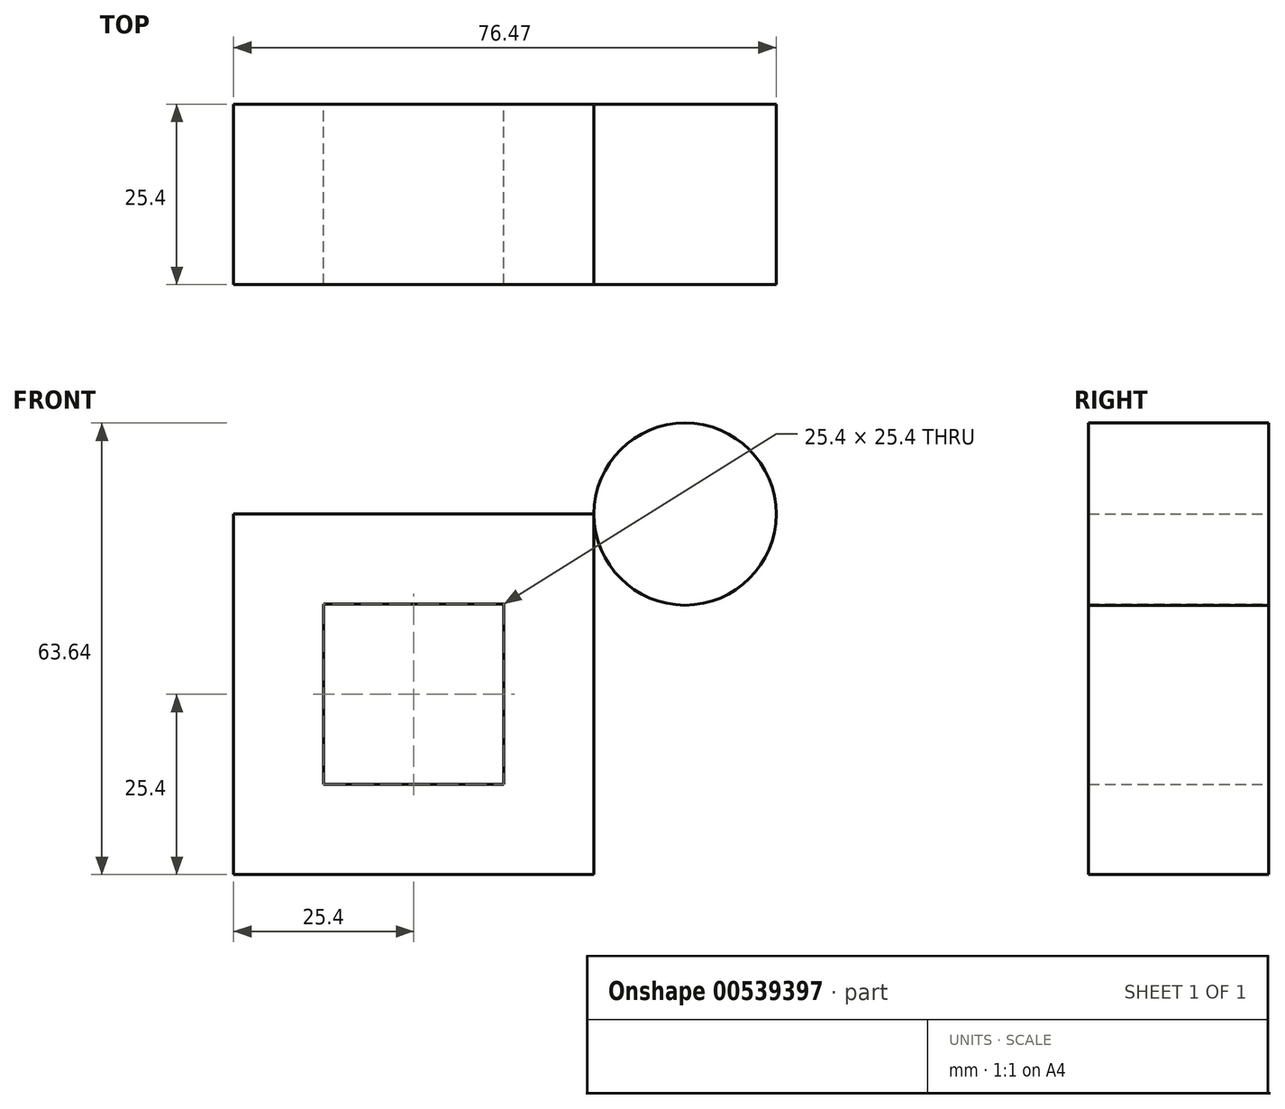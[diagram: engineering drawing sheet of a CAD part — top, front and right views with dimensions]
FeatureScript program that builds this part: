
annotation { "Feature Type Name" : "Feature", "Feature Type Description" : "" }
export const myFeature = defineFeature(function(context is Context, id is Id, definition is map)
    precondition{}
    {
        {
            var Q0;
            Q0=qCreatedBy(makeId("Front.planeOp"),FACE);
            var sketch = newSketch(context, id + "F0", { "sketchPlane" : qUnion([Q0])});
            skLineSegment(sketch, "E0.bottom", {"start": v(0, 50.8) * mm, "end": v(50.8, 50.8) * mm});
            skLineSegment(sketch, "E0.top", {"start": v(0, 0) * mm, "end": v(50.8, 0) * mm});
            skLineSegment(sketch, "E0.left", {"start": v(0, 50.8) * mm, "end": v(0, 0) * mm});
            skLineSegment(sketch, "E0.right", {"start": v(50.8, 50.8) * mm, "end": v(50.8, 0) * mm});
            skCircle(sketch, "E1", {"center": v(63.64, 50.8) * mm, "radius": 12.84 * mm});
            skLineSegment(sketch, "E2.bottom", {"start": v(38.1, 12.7) * mm, "end": v(12.7, 12.7) * mm});
            skLineSegment(sketch, "E2.top", {"start": v(38.1, 38.1) * mm, "end": v(12.7, 38.1) * mm});
            skLineSegment(sketch, "E2.left", {"start": v(38.1, 12.7) * mm, "end": v(38.1, 38.1) * mm});
            skLineSegment(sketch, "E2.right", {"start": v(12.7, 12.7) * mm, "end": v(12.7, 38.1) * mm});
            skPoint(sketch, "E2.middle", {"position": v(25.4, 25.4) * mm});
            skPoint(sketch, "E2.middle.positionSnap0", {"position": v(25.4, 50.8) * mm});
            skPoint(sketch, "E2.middle.positionSnap1", {"position": v(0, 25.4) * mm});
            skPoint(sketch, "E2.centerSnap0", {"position": v(25.4, 50.8) * mm});
            skPoint(sketch, "E2.centerSnap1", {"position": v(0, 25.4) * mm});
            skLineSegment(sketch, "E3", {"start": v(0, 0) * mm, "end": v(50.8, 50.8) * mm, "construction": true});
            skLineSegment(sketch, "E4", {"start": v(0, 50.8) * mm, "end": v(50.8, 0) * mm, "construction": true});
            skSolve(sketch);
        }
        {
            var Q0;
            Q0 = qSketchRegion(id + "F0", true);
            extrude(context, id + "F1", {"entities" : qUnion([Q0]), "depth" : 25.4 * mm, "offsetDistance" : 25.4 * mm});
        }
    });
